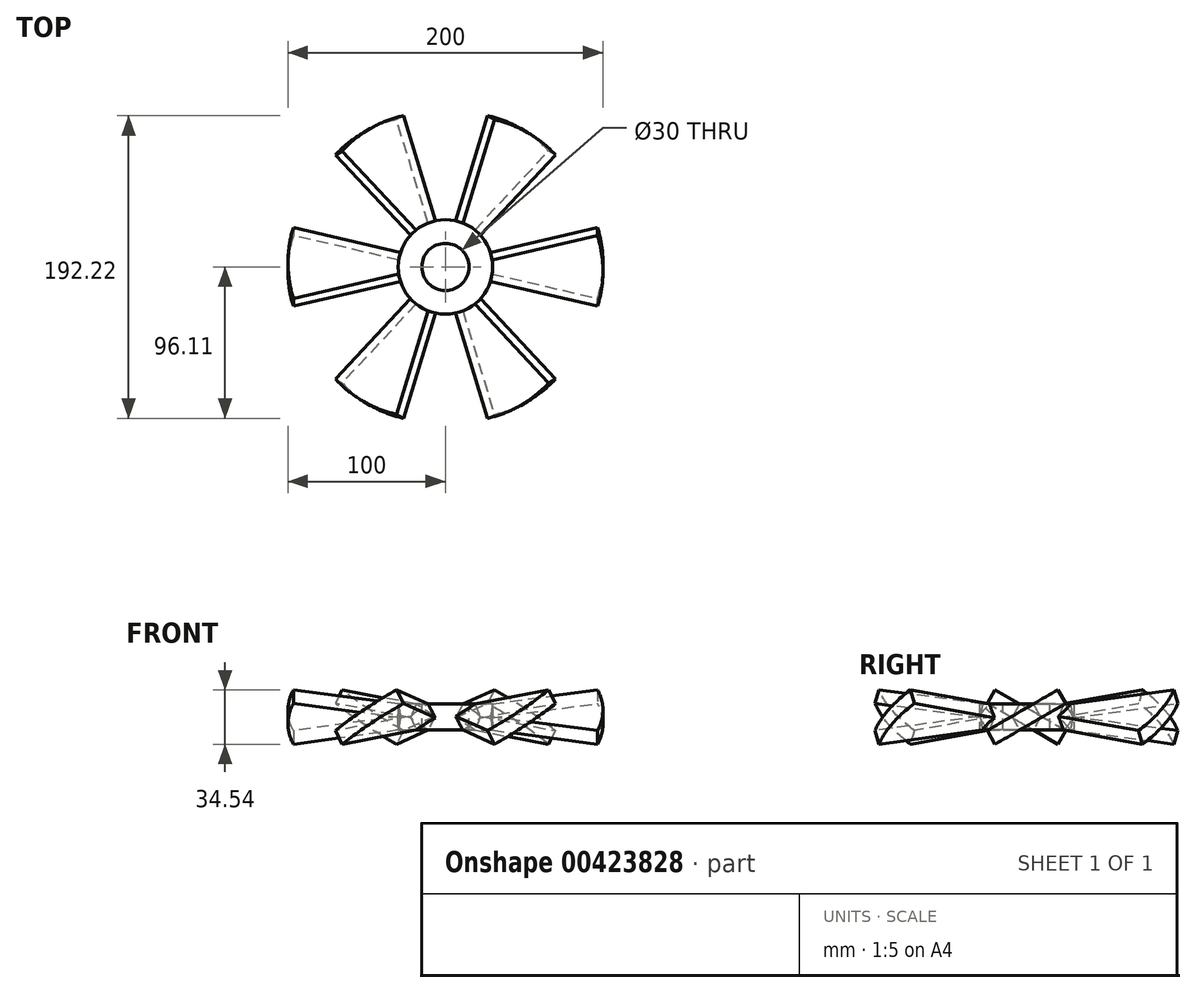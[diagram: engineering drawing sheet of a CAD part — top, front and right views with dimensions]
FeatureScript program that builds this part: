
annotation { "Feature Type Name" : "Feature", "Feature Type Description" : "" }
export const myFeature = defineFeature(function(context is Context, id is Id, definition is map)
    precondition{}
    {
        {
            var Q0;
            Q0=qCreatedBy(makeId("Top.planeOp"),FACE);
            var sketch = newSketch(context, id + "F0", { "sketchPlane" : qUnion([Q0])});
            skArc(sketch, "E0", {"start": v(96.6, -25.88) * mm, "mid": v(100, 0) * mm, "end": v(96.6, 25.88) * mm});
            skLineSegment(sketch, "E1", {"start": v(0, 0) * mm, "end": v(96.6, 25.88) * mm});
            skLineSegment(sketch, "E2.MirrorCS", {"start": v(0, 0) * mm, "end": v(96.6, -25.88) * mm});
            skSolve(sketch);
        }
        {
            var Q0;
            Q0=makeQuery(id+"F0.imprint","IMPRINT",FACE,{"disambiguationData":[TD([[makeQuery(id+"F0.imprint","IMPRINT",EDGE,{"derivedFrom":sQuery(id+"F0.wireOp",EDGE,"E0")}),1.0]])]});
            extrude(context, id + "F1", {"entities" : qUnion([Q0]), "endBound" : BoundingType.SYMMETRIC, "depth" : 10 * mm});
        }
        {
            var Q0;
            Q0=qCreatedBy(makeId("Top.planeOp"),FACE);
            var sketch = newSketch(context, id + "F2", { "sketchPlane" : qUnion([Q0])});
            skLineSegment(sketch, "E3", {"start": v(0, 0) * mm, "end": v(156.33, 0) * mm});
            skSolve(sketch);
        }
        {
            var Q0;
            Q0=makeQuery(id+"F1.opExtrude","SWEPT_BODY",BODY,{"disambiguationData":[OSD([sQuery(id+"F0.wireOp",EDGE,"E0"),sQuery(id+"F0.wireOp",EDGE,"E1"),sQuery(id+"F0.wireOp",EDGE,"E2.MirrorCS")])]});
            var Q1;
            Q1=sQuery(id+"F2.wireOp",EDGE,"E3");
            transform(context, id + "F3", {"entities" : qUnion([Q0]), "transformType" : TransformType.ROTATION, "transformAxis" : qUnion([Q1]), "angle" : 30 * degree, "makeCopy" : false});
        }
        {
            var Q0;
            Q0=qCreatedBy(makeId("Right.planeOp"),FACE);
            var sketch = newSketch(context, id + "F4", { "sketchPlane" : qUnion([Q0])});
            skLineSegment(sketch, "E4", {"start": v(0, 0) * mm, "end": v(0, 83.34) * mm});
            skSolve(sketch);
        }
        {
            var Q0;
            Q0=makeQuery(id+"F1.opExtrude","SWEPT_BODY",BODY,{"disambiguationData":[OSD([sQuery(id+"F0.wireOp",EDGE,"E0"),sQuery(id+"F0.wireOp",EDGE,"E1"),sQuery(id+"F0.wireOp",EDGE,"E2.MirrorCS")])]});
            var Q1;
            Q1=sQuery(id+"F4.wireOp",EDGE,"E4");
            circularPattern(context, id + "F5", {"entities" : qUnion([Q0]), "axis" : qUnion([Q1]), "angle" : 360 * degree, "instanceCount" : 6, "equalSpace" : true});
        }
        {
            var Q0;
            Q0=qCreatedBy(makeId("Top.planeOp"),FACE);
            var sketch = newSketch(context, id + "F6", { "sketchPlane" : qUnion([Q0])});
            skCircle(sketch, "E5", {"center": v(0, 0) * mm, "radius": 30 * mm});
            skSolve(sketch);
        }
        {
            var Q0;
            Q0=qSketchRegion(id+"F6",true);
            extrude(context, id + "F7", {"entities" : qUnion([Q0]), "operationType" : NewBodyOperationType.REMOVE, "endBound" : BoundingType.SYMMETRIC, "oppositeDirection" : true, "depth" : 25 * mm});
        }
        {
            var Q0;
            Q0=qSketchRegion(id+"F6",true);
            var Q1;
            {var subQ0=sQuery(id+"F0.wireOp",EDGE,"E1");Q1=makeQuery(id+"F7.boolean.opBoolean","INTERSECT",VERTEX,{"derivedFrom":[makeQuery(id+"F5.opPattern","COPY",FACE,{"derivedFrom":makeQuery(id+"F1.opExtrude","CAP_FACE",FACE,{"disambiguationData":[OSD([sQuery(id+"F0.wireOp",EDGE,"E0"),subQ0,sQuery(id+"F0.wireOp",EDGE,"E2.MirrorCS")])],"isStart":false}),"instanceName":"2"}),makeQuery(id+"F5.opPattern","COPY",FACE,{"derivedFrom":makeQuery(id+"F1.opExtrude","SWEPT_FACE",FACE,{"disambiguationData":[OSD([subQ0])]}),"instanceName":"2"}),makeQuery(id+"F7.opExtrude","SWEPT_FACE",FACE,{"disambiguationData":[OSD([sQuery(id+"F6.wireOp",EDGE,"E5")])]})]});}
            var Q2;
            {var subQ0=sQuery(id+"F0.wireOp",EDGE,"E2.MirrorCS");Q2=makeQuery(id+"F7.boolean.opBoolean","INTERSECT",VERTEX,{"derivedFrom":[makeQuery(id+"F5.opPattern","COPY",FACE,{"derivedFrom":makeQuery(id+"F1.opExtrude","CAP_FACE",FACE,{"disambiguationData":[OSD([sQuery(id+"F0.wireOp",EDGE,"E0"),sQuery(id+"F0.wireOp",EDGE,"E1"),subQ0])],"isStart":true}),"instanceName":"5"}),makeQuery(id+"F5.opPattern","COPY",FACE,{"derivedFrom":makeQuery(id+"F1.opExtrude","SWEPT_FACE",FACE,{"disambiguationData":[OSD([subQ0])]}),"instanceName":"5"}),makeQuery(id+"F7.opExtrude","SWEPT_FACE",FACE,{"disambiguationData":[OSD([sQuery(id+"F6.wireOp",EDGE,"E5")])]})]});}
            extrude(context, id + "F8", {"entities" : qUnion([Q0]), "endBound" : BoundingType.UP_TO_VERTEX, "endBoundEntityVertex" : qUnion([Q1]), "depth" : 25 * mm, "hasSecondDirection" : true, "secondDirectionBound" : SecondDirectionBoundingType.UP_TO_VERTEX, "secondDirectionOppositeDirection" : true, "secondDirectionBoundEntityVertex" : qUnion([Q2]), "secondDirectionDepth" : 25 * mm});
        }
        {
            var Q0;
            Q0=makeQuery(id+"F8.opExtrude","CAP_FACE",FACE,{"disambiguationData":[OSD([sQuery(id+"F6.wireOp",EDGE,"E5")])],"isStart":false});
            var sketch = newSketch(context, id + "F9", { "sketchPlane" : qUnion([Q0])});
            skCircle(sketch, "E6", {"center": v(0, 0) * mm, "radius": 15 * mm});
            skSolve(sketch);
        }
        {
            var Q0;
            Q0=qSketchRegion(id+"F9",true);
            extrude(context, id + "F10", {"entities" : qUnion([Q0]), "operationType" : NewBodyOperationType.REMOVE, "oppositeDirection" : true, "depth" : 25 * mm});
        }
    });
